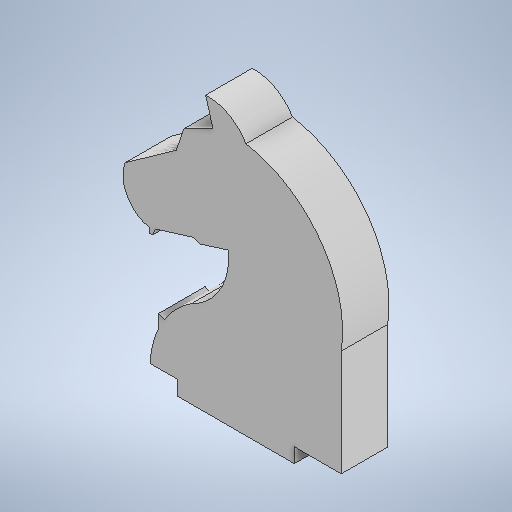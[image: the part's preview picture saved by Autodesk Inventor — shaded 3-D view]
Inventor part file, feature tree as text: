
AUTODESK INVENTOR PART (.ipt)
format: ipt  version: 2025.1 (Build 291241000, 241)  size: 304,128 bytes
history: native  units: mm
features: other x2, extrude x1, sketch x1
ambient origin geometry x8: Origin, YZ Plane, XZ Plane, XY Plane, X Axis, Y Axis, Z Axis, Center Point
bodies: Body1 (feature_tree)
feature tree (4):
  other  "Sólido1"
  extrude  "Extrusión1"  Depth=10.0mm
  sketch  "Boceto1"  dims[d5=10.0mm d6=0.0mm d8=14.0mm d12=0.346266mm]
  other  "Imagen1"
